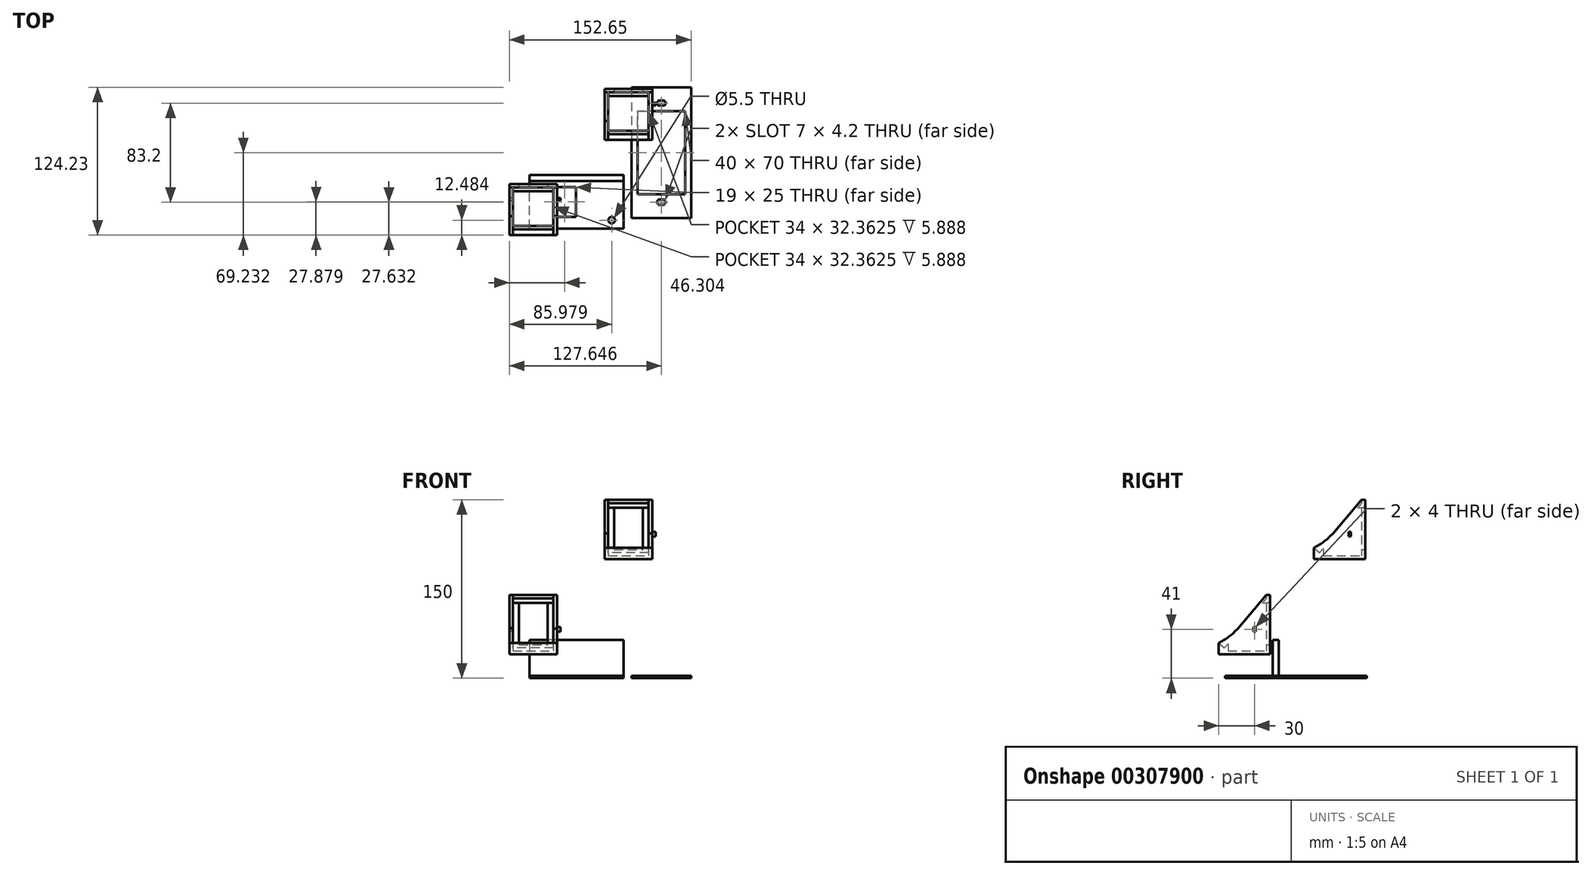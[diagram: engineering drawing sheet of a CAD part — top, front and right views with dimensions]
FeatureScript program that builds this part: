
annotation { "Feature Type Name" : "Feature", "Feature Type Description" : "" }
export const myFeature = defineFeature(function(context is Context, id is Id, definition is map)
    precondition{}
    {
        {
            var Q0;
            Q0=qCreatedBy(makeId("Front.planeOp"),FACE);
            var sketch = newSketch(context, id + "F0", { "sketchPlane" : qUnion([Q0])});
            skLineSegment(sketch, "E0.bottom", {"start": v(-60, 70) * mm, "end": v(-20, 70) * mm});
            skLineSegment(sketch, "E0.top", {"start": v(-60, 20) * mm, "end": v(-20, 20) * mm});
            skLineSegment(sketch, "E0.left", {"start": v(-60, 70) * mm, "end": v(-60, 20) * mm});
            skLineSegment(sketch, "E0.right", {"start": v(-20, 70) * mm, "end": v(-20, 20) * mm});
            skLineSegment(sketch, "E1.bottom", {"start": v(-52, 66) * mm, "end": v(-28, 66) * mm});
            skLineSegment(sketch, "E1.top", {"start": v(-52, 28) * mm, "end": v(-28, 28) * mm});
            skLineSegment(sketch, "E1.left", {"start": v(-52, 66) * mm, "end": v(-52, 28) * mm});
            skLineSegment(sketch, "E1.right", {"start": v(-28, 66) * mm, "end": v(-28, 28) * mm});
            skSolve(sketch);
        }
        {
            var Q0;
            Q0 = qSketchRegion(id + "F0", true);
            extrude(context, id + "F1", {"entities" : qUnion([Q0]), "depth" : 3 * mm});
        }
        {
            var Q0;
            Q0=makeQuery(id+"F1.opExtrude","CAP_FACE",FACE,{"disambiguationData":[OSD([sQuery(id+"F0.wireOp",EDGE,"E0.bottom"),sQuery(id+"F0.wireOp",EDGE,"E0.top"),sQuery(id+"F0.wireOp",EDGE,"E0.left"),sQuery(id+"F0.wireOp",EDGE,"E0.right"),sQuery(id+"F0.wireOp",EDGE,"E1.bottom"),sQuery(id+"F0.wireOp",EDGE,"E1.top"),sQuery(id+"F0.wireOp",EDGE,"E1.left"),sQuery(id+"F0.wireOp",EDGE,"E1.right")])],"isStart":false});
            var sketch = newSketch(context, id + "F2", { "sketchPlane" : qUnion([Q0])});
            skPoint(sketch, "E2.left.start.orphan", {"position": v(-60, 28) * mm});
            skLineSegment(sketch, "E3.bottom", {"start": v(-60, 23) * mm, "end": v(-20, 23) * mm});
            skLineSegment(sketch, "E3.top", {"start": v(-60, 20) * mm, "end": v(-20, 20) * mm});
            skLineSegment(sketch, "E3.left", {"start": v(-60, 23) * mm, "end": v(-60, 20) * mm});
            skLineSegment(sketch, "E3.right", {"start": v(-20, 23) * mm, "end": v(-20, 20) * mm});
            skSolve(sketch);
        }
        {
            var Q0;
            Q0 = qSketchRegion(id + "F2", true);
            extrude(context, id + "F3", {"entities" : qUnion([Q0]), "operationType" : NewBodyOperationType.ADD, "depth" : 40 * mm});
        }
        {
            var Q0;
            Q0=makeQuery(id+"F3.boolean.opBoolean","MERGE",FACE,{"derivedFrom":[makeQuery(id+"F1.opExtrude","SWEPT_FACE",FACE,{"disambiguationData":[OSD([sQuery(id+"F0.wireOp",EDGE,"E0.left")])]}),makeQuery(id+"F3.opExtrude","SWEPT_FACE",FACE,{"disambiguationData":[OSD([sQuery(id+"F2.wireOp",EDGE,"E3.left")])]})]});
            var sketch = newSketch(context, id + "F4", { "sketchPlane" : qUnion([Q0])});
            skLineSegment(sketch, "E4", {"start": v(3, 70) * mm, "end": v(43, 23) * mm});
            skSolve(sketch);
        }
        {
            var Q0;
            Q0=makeQuery(id+"F4.imprint","IMPRINT",FACE,{"disambiguationData":[TD([[makeQuery(id+"F4.imprint","IMPRINT",EDGE,{"derivedFrom":sQuery(id+"F4.wireOp",EDGE,"E4")}),-1.0]])]});
            extrude(context, id + "F5", {"entities" : qUnion([Q0]), "operationType" : NewBodyOperationType.ADD, "oppositeDirection" : true, "depth" : 3 * mm});
        }
        {
            var Q0;
            Q0=makeQuery(id+"F3.boolean.opBoolean","MERGE",FACE,{"derivedFrom":[makeQuery(id+"F1.opExtrude","SWEPT_FACE",FACE,{"disambiguationData":[OSD([sQuery(id+"F0.wireOp",EDGE,"E0.right")])]}),makeQuery(id+"F3.opExtrude","SWEPT_FACE",FACE,{"disambiguationData":[OSD([sQuery(id+"F2.wireOp",EDGE,"E3.right")])]})]});
            var sketch = newSketch(context, id + "F6", { "sketchPlane" : qUnion([Q0])});
            skLineSegment(sketch, "E5", {"start": v(-43, 23) * mm, "end": v(-3, 70) * mm});
            skSolve(sketch);
        }
        {
            var Q0;
            Q0=makeQuery(id+"F6.imprint","IMPRINT",FACE,{"disambiguationData":[TD([[makeQuery(id+"F6.imprint","IMPRINT",EDGE,{"derivedFrom":sQuery(id+"F6.wireOp",EDGE,"E5")}),-1.0]])]});
            extrude(context, id + "F7", {"entities" : qUnion([Q0]), "operationType" : NewBodyOperationType.ADD, "oppositeDirection" : true, "depth" : 3 * mm});
        }
        {
            var Q0;
            Q0=makeQuery(id+"F5.opExtrude","CAP_FACE",FACE,{"disambiguationData":[OSD([sQuery(id+"F0.wireOp",EDGE,"E0.left"),sQuery(id+"F2.wireOp",EDGE,"E3.bottom"),sQuery(id+"F2.wireOp",EDGE,"E3.left"),sQuery(id+"F4.wireOp",EDGE,"E4")])],"isStart":false});
            var sketch = newSketch(context, id + "F8", { "sketchPlane" : qUnion([Q0])});
            skLineSegment(sketch, "E6", {"start": v(-3, 66.91) * mm, "end": v(-6.24, 63.1) * mm});
            skLineSegment(sketch, "E7", {"start": v(-6.24, 63.1) * mm, "end": v(-3, 63.1) * mm});
            skLineSegment(sketch, "E8", {"start": v(-3, 63.1) * mm, "end": v(-3, 66.91) * mm});
            skLineSegment(sketch, "E9.0", {"start": v(-3, 66) * mm, "end": v(0, 66) * mm});
            skLineSegment(sketch, "E10", {"start": v(-3, 63.1) * mm, "end": v(0, 63.1) * mm});
            skLineSegment(sketch, "E11", {"start": v(0, 63.1) * mm, "end": v(0, 66) * mm});
            skSolve(sketch);
        }
        {
            var Q0;
            Q0 = qSketchRegion(id + "F8", true);
            var Q1;
            Q1=makeQuery(id+"F7.opExtrude","CAP_FACE",FACE,{"disambiguationData":[OSD([sQuery(id+"F0.wireOp",EDGE,"E0.right"),sQuery(id+"F2.wireOp",EDGE,"E3.bottom"),sQuery(id+"F2.wireOp",EDGE,"E3.right"),sQuery(id+"F6.wireOp",EDGE,"E5")])],"isStart":false});
            extrude(context, id + "F9", {"entities" : qUnion([Q0]), "operationType" : NewBodyOperationType.ADD, "endBound" : BoundingType.UP_TO_SURFACE, "endBoundEntityFace" : qUnion([Q1]), "depth" : 25 * mm});
        }
        {
            var Q0;
            Q0=makeQuery(id+"F5.opExtrude","CAP_FACE",FACE,{"disambiguationData":[OSD([sQuery(id+"F0.wireOp",EDGE,"E0.left"),sQuery(id+"F2.wireOp",EDGE,"E3.bottom"),sQuery(id+"F2.wireOp",EDGE,"E3.left"),sQuery(id+"F4.wireOp",EDGE,"E4")])],"isStart":false});
            var sketch = newSketch(context, id + "F10", { "sketchPlane" : qUnion([Q0])});
            skLineSegment(sketch, "E12", {"start": v(-35.36, 23) * mm, "end": v(-43, 29.5) * mm});
            skLineSegment(sketch, "E13", {"start": v(-43, 29.5) * mm, "end": v(-43, 23) * mm});
            skLineSegment(sketch, "E14", {"start": v(-43, 23) * mm, "end": v(-35.36, 23) * mm});
            skSolve(sketch);
        }
        {
            var Q0;
            Q0 = qSketchRegion(id + "F10", true);
            var Q1;
            {var subQ0=sQuery(id+"F2.wireOp",EDGE,"E3.right");var subQ1=sQuery(id+"F0.wireOp",EDGE,"E0.right");Q1=makeQuery(id+"F7.boolean.opBoolean","MERGE",FACE,{"derivedFrom":[makeQuery(id+"F3.boolean.opBoolean","MERGE",FACE,{"derivedFrom":[makeQuery(id+"F1.opExtrude","SWEPT_FACE",FACE,{"disambiguationData":[OSD([subQ1])]}),makeQuery(id+"F3.opExtrude","SWEPT_FACE",FACE,{"disambiguationData":[OSD([subQ0])]})]}),makeQuery(id+"F7.opExtrude","CAP_FACE",FACE,{"disambiguationData":[OSD([subQ1,sQuery(id+"F2.wireOp",EDGE,"E3.bottom"),subQ0,sQuery(id+"F6.wireOp",EDGE,"E5")])],"isStart":true})]});}
            var Q2;
            {var subQ0=sQuery(id+"F2.wireOp",EDGE,"E3.left");var subQ1=sQuery(id+"F0.wireOp",EDGE,"E0.left");Q2=makeQuery(id+"F5.boolean.opBoolean","MERGE",FACE,{"derivedFrom":[makeQuery(id+"F3.boolean.opBoolean","MERGE",FACE,{"derivedFrom":[makeQuery(id+"F1.opExtrude","SWEPT_FACE",FACE,{"disambiguationData":[OSD([subQ1])]}),makeQuery(id+"F3.opExtrude","SWEPT_FACE",FACE,{"disambiguationData":[OSD([subQ0])]})]}),makeQuery(id+"F5.opExtrude","CAP_FACE",FACE,{"disambiguationData":[OSD([subQ1,sQuery(id+"F2.wireOp",EDGE,"E3.bottom"),subQ0,sQuery(id+"F4.wireOp",EDGE,"E4")])],"isStart":true})]});}
            extrude(context, id + "F11", {"entities" : qUnion([Q0]), "operationType" : NewBodyOperationType.ADD, "endBound" : BoundingType.UP_TO_SURFACE, "endBoundEntityFace" : qUnion([Q1]), "depth" : 25 * mm, "hasSecondDirection" : true, "secondDirectionBound" : SecondDirectionBoundingType.UP_TO_SURFACE, "secondDirectionOppositeDirection" : true, "secondDirectionBoundEntityFace" : qUnion([Q2]), "secondDirectionDepth" : 25 * mm});
        }
        {
            var Q0;
            Q0=makeQuery(id+"F5.opExtrude","CAP_FACE",FACE,{"disambiguationData":[OSD([sQuery(id+"F0.wireOp",EDGE,"E0.left"),sQuery(id+"F2.wireOp",EDGE,"E3.bottom"),sQuery(id+"F2.wireOp",EDGE,"E3.left"),sQuery(id+"F4.wireOp",EDGE,"E4")])],"isStart":false});
            var sketch = newSketch(context, id + "F12", { "sketchPlane" : qUnion([Q0])});
            skLineSegment(sketch, "E15", {"start": v(-38.27, 25.47) * mm, "end": v(-35.36, 28.89) * mm});
            skLineSegment(sketch, "E16", {"start": v(-35.36, 28.89) * mm, "end": v(-35.36, 23) * mm});
            skSolve(sketch);
        }
        {
            var Q0;
            {var subQ0=sQuery(id+"F12.wireOp",EDGE,"E15");Q0=makeQuery(id+"F12.imprint","IMPRINT",FACE,{"disambiguationData":[TD([[makeQuery(id+"F12.imprint","IMPRINT",EDGE,{"derivedFrom":subQ0}),-1.0]])]});}
            var Q1;
            Q1=makeQuery(id+"F7.opExtrude","CAP_FACE",FACE,{"disambiguationData":[OSD([sQuery(id+"F0.wireOp",EDGE,"E0.right"),sQuery(id+"F2.wireOp",EDGE,"E3.bottom"),sQuery(id+"F2.wireOp",EDGE,"E3.right"),sQuery(id+"F6.wireOp",EDGE,"E5")])],"isStart":false});
            extrude(context, id + "F13", {"entities" : qUnion([Q0]), "operationType" : NewBodyOperationType.ADD, "endBound" : BoundingType.UP_TO_SURFACE, "endBoundEntityFace" : qUnion([Q1]), "depth" : 25 * mm});
        }
        {
            var Q0;
            {var subQ0=sQuery(id+"F6.wireOp",EDGE,"E5");var subQ1=sQuery(id+"F2.wireOp",EDGE,"E3.right");var subQ2=sQuery(id+"F2.wireOp",EDGE,"E3.bottom");var subQ3=sQuery(id+"F0.wireOp",EDGE,"E0.right");Q0=makeQuery(id+"F11.boolean.opBoolean","MERGE",FACE,{"derivedFrom":[makeQuery(id+"F7.boolean.opBoolean","MERGE",FACE,{"derivedFrom":[makeQuery(id+"F3.boolean.opBoolean","MERGE",FACE,{"derivedFrom":[makeQuery(id+"F1.opExtrude","SWEPT_FACE",FACE,{"disambiguationData":[OSD([subQ3])]}),makeQuery(id+"F3.opExtrude","SWEPT_FACE",FACE,{"disambiguationData":[OSD([subQ1])]})]}),makeQuery(id+"F7.opExtrude","CAP_FACE",FACE,{"disambiguationData":[OSD([subQ3,subQ2,subQ1,subQ0])],"isStart":true})]}),makeQuery(id+"F11.opExtrude","CAP_FACE",FACE,{"disambiguationData":[OSD([subQ3,subQ2,subQ1,subQ0])],"isStart":false})]});}
            var sketch = newSketch(context, id + "F14", { "sketchPlane" : qUnion([Q0])});
            skLineSegment(sketch, "E17.bottom", {"start": v(-14, 43) * mm, "end": v(-12, 43) * mm});
            skLineSegment(sketch, "E17.top", {"start": v(-14, 39) * mm, "end": v(-12, 39) * mm});
            skLineSegment(sketch, "E17.left", {"start": v(-14, 43) * mm, "end": v(-14, 39) * mm});
            skLineSegment(sketch, "E17.right", {"start": v(-12, 43) * mm, "end": v(-12, 39) * mm});
            skSolve(sketch);
        }
        {
            var Q0;
            Q0 = qSketchRegion(id + "F14", true);
            extrude(context, id + "F15", {"entities" : qUnion([Q0]), "operationType" : NewBodyOperationType.ADD, "depth" : 3 * mm});
        }
        {
            var Q0;
            {var subQ0=sQuery(id+"F4.wireOp",EDGE,"E4");var subQ1=sQuery(id+"F2.wireOp",EDGE,"E3.left");var subQ2=sQuery(id+"F2.wireOp",EDGE,"E3.bottom");var subQ3=sQuery(id+"F0.wireOp",EDGE,"E0.left");Q0=makeQuery(id+"F11.boolean.opBoolean","MERGE",FACE,{"derivedFrom":[makeQuery(id+"F5.boolean.opBoolean","MERGE",FACE,{"derivedFrom":[makeQuery(id+"F3.boolean.opBoolean","MERGE",FACE,{"derivedFrom":[makeQuery(id+"F1.opExtrude","SWEPT_FACE",FACE,{"disambiguationData":[OSD([subQ3])]}),makeQuery(id+"F3.opExtrude","SWEPT_FACE",FACE,{"disambiguationData":[OSD([subQ1])]})]}),makeQuery(id+"F5.opExtrude","CAP_FACE",FACE,{"disambiguationData":[OSD([subQ3,subQ2,subQ1,subQ0])],"isStart":true})]}),makeQuery(id+"F11.opExtrude","CAP_FACE",FACE,{"disambiguationData":[OSD([subQ3,subQ2,subQ1,subQ0])],"isStart":true})]});}
            var sketch = newSketch(context, id + "F16", { "sketchPlane" : qUnion([Q0])});
            skLineSegment(sketch, "E18.bottom", {"start": v(12, 43) * mm, "end": v(14, 43) * mm});
            skLineSegment(sketch, "E18.top", {"start": v(12, 39) * mm, "end": v(14, 39) * mm});
            skLineSegment(sketch, "E18.left", {"start": v(12, 43) * mm, "end": v(12, 39) * mm});
            skLineSegment(sketch, "E18.right", {"start": v(14, 43) * mm, "end": v(14, 39) * mm});
            skSolve(sketch);
        }
        {
            var Q0;
            Q0 = qSketchRegion(id + "F16", true);
            extrude(context, id + "F17", {"entities" : qUnion([Q0]), "operationType" : NewBodyOperationType.REMOVE, "oppositeDirection" : true, "depth" : 25 * mm});
        }
        {
            var Q0;
            {var subQ0=sQuery(id+"F4.wireOp",EDGE,"E4");var subQ1=sQuery(id+"F2.wireOp",EDGE,"E3.left");var subQ2=sQuery(id+"F2.wireOp",EDGE,"E3.bottom");var subQ3=sQuery(id+"F0.wireOp",EDGE,"E0.left");Q0=makeQuery(id+"F11.boolean.opBoolean","MERGE",FACE,{"derivedFrom":[makeQuery(id+"F5.boolean.opBoolean","MERGE",FACE,{"derivedFrom":[makeQuery(id+"F3.boolean.opBoolean","MERGE",FACE,{"derivedFrom":[makeQuery(id+"F1.opExtrude","SWEPT_FACE",FACE,{"disambiguationData":[OSD([subQ3])]}),makeQuery(id+"F3.opExtrude","SWEPT_FACE",FACE,{"disambiguationData":[OSD([subQ1])]})]}),makeQuery(id+"F5.opExtrude","CAP_FACE",FACE,{"disambiguationData":[OSD([subQ3,subQ2,subQ1,subQ0])],"isStart":true})]}),makeQuery(id+"F11.opExtrude","CAP_FACE",FACE,{"disambiguationData":[OSD([subQ3,subQ2,subQ1,subQ0])],"isStart":true})]});}
            var sketch = newSketch(context, id + "F18", { "sketchPlane" : qUnion([Q0])});
            skArc(sketch, "E19", {"start": v(27.03, 41.77) * mm, "mid": v(34.47, 34.92) * mm, "end": v(43, 29.5) * mm});
            skSolve(sketch);
        }
        {
            var Q0;
            {var subQ0=sQuery(id+"F18.wireOp",EDGE,"E19");Q0=makeQuery(id+"F18.imprint","IMPRINT",FACE,{"disambiguationData":[TD([[makeQuery(id+"F18.imprint","IMPRINT",EDGE,{"derivedFrom":subQ0}),-1.0]])]});}
            var Q1;
            Q1=makeQuery(id+"F5.opExtrude","CAP_FACE",FACE,{"disambiguationData":[OSD([sQuery(id+"F0.wireOp",EDGE,"E0.left"),sQuery(id+"F2.wireOp",EDGE,"E3.bottom"),sQuery(id+"F2.wireOp",EDGE,"E3.left"),sQuery(id+"F4.wireOp",EDGE,"E4")])],"isStart":false});
            extrude(context, id + "F19", {"entities" : qUnion([Q0]), "operationType" : NewBodyOperationType.ADD, "endBound" : BoundingType.UP_TO_SURFACE, "oppositeDirection" : true, "endBoundEntityFace" : qUnion([Q1]), "depth" : 25 * mm});
        }
        {
            var Q0;
            {var subQ0=sQuery(id+"F6.wireOp",EDGE,"E5");var subQ1=sQuery(id+"F2.wireOp",EDGE,"E3.right");var subQ2=sQuery(id+"F2.wireOp",EDGE,"E3.bottom");var subQ3=sQuery(id+"F0.wireOp",EDGE,"E0.right");Q0=makeQuery(id+"F11.boolean.opBoolean","MERGE",FACE,{"derivedFrom":[makeQuery(id+"F7.boolean.opBoolean","MERGE",FACE,{"derivedFrom":[makeQuery(id+"F3.boolean.opBoolean","MERGE",FACE,{"derivedFrom":[makeQuery(id+"F1.opExtrude","SWEPT_FACE",FACE,{"disambiguationData":[OSD([subQ3])]}),makeQuery(id+"F3.opExtrude","SWEPT_FACE",FACE,{"disambiguationData":[OSD([subQ1])]})]}),makeQuery(id+"F7.opExtrude","CAP_FACE",FACE,{"disambiguationData":[OSD([subQ3,subQ2,subQ1,subQ0])],"isStart":true})]}),makeQuery(id+"F11.opExtrude","CAP_FACE",FACE,{"disambiguationData":[OSD([subQ3,subQ2,subQ1,subQ0])],"isStart":false})]});}
            var sketch = newSketch(context, id + "F20", { "sketchPlane" : qUnion([Q0])});
            skArc(sketch, "E20.0", {"start": v(-43, 29.5) * mm, "mid": v(-34.47, 34.92) * mm, "end": v(-27.03, 41.77) * mm});
            skLineSegment(sketch, "E21.0", {"start": v(-39.8, 26.77) * mm, "end": v(-3, 70) * mm});
            skLineSegment(sketch, "E22.0", {"start": v(-39.8, 26.77) * mm, "end": v(-43, 29.5) * mm});
            skSolve(sketch);
        }
        {
            var Q0;
            Q0 = qSketchRegion(id + "F20", true);
            var Q1;
            Q1=makeQuery(id+"F7.opExtrude","CAP_FACE",FACE,{"disambiguationData":[OSD([sQuery(id+"F0.wireOp",EDGE,"E0.right"),sQuery(id+"F2.wireOp",EDGE,"E3.bottom"),sQuery(id+"F2.wireOp",EDGE,"E3.right"),sQuery(id+"F6.wireOp",EDGE,"E5")])],"isStart":false});
            extrude(context, id + "F21", {"entities" : qUnion([Q0]), "operationType" : NewBodyOperationType.ADD, "endBound" : BoundingType.UP_TO_SURFACE, "oppositeDirection" : true, "endBoundEntityFace" : qUnion([Q1]), "depth" : 25 * mm});
        }
        {
            var Q0;
            Q0=makeQuery(id+"F1.opExtrude","SWEPT_BODY",BODY,{"disambiguationData":[OSD([sQuery(id+"F0.wireOp",EDGE,"E0.bottom"),sQuery(id+"F0.wireOp",EDGE,"E0.top"),sQuery(id+"F0.wireOp",EDGE,"E0.left"),sQuery(id+"F0.wireOp",EDGE,"E0.right"),sQuery(id+"F0.wireOp",EDGE,"E1.bottom"),sQuery(id+"F0.wireOp",EDGE,"E1.top"),sQuery(id+"F0.wireOp",EDGE,"E1.left"),sQuery(id+"F0.wireOp",EDGE,"E1.right")])]});
            transform(context, id + "F22", {"entities" : qUnion([Q0]), "transformType" : TransformType.TRANSLATION_3D, "dx" : 80 * mm, "dy" : 80 * mm, "dz" : 80 * mm, "makeCopy" : true});
        }
        {
            var Q0;
            {var subQ0=sQuery(id+"F4.wireOp",EDGE,"E4");var subQ1=sQuery(id+"F2.wireOp",EDGE,"E3.left");var subQ2=sQuery(id+"F2.wireOp",EDGE,"E3.bottom");var subQ3=sQuery(id+"F0.wireOp",EDGE,"E0.left");Q0=makeQuery(id+"F22.opPattern","COPY",FACE,{"derivedFrom":makeQuery(id+"F19.boolean.opBoolean","MERGE",FACE,{"derivedFrom":[makeQuery(id+"F11.boolean.opBoolean","MERGE",FACE,{"derivedFrom":[makeQuery(id+"F5.boolean.opBoolean","MERGE",FACE,{"derivedFrom":[makeQuery(id+"F3.boolean.opBoolean","MERGE",FACE,{"derivedFrom":[makeQuery(id+"F1.opExtrude","SWEPT_FACE",FACE,{"disambiguationData":[OSD([subQ3])]}),makeQuery(id+"F3.opExtrude","SWEPT_FACE",FACE,{"disambiguationData":[OSD([subQ1])]})]}),makeQuery(id+"F5.opExtrude","CAP_FACE",FACE,{"disambiguationData":[OSD([subQ3,subQ2,subQ1,subQ0])],"isStart":true})]}),makeQuery(id+"F11.opExtrude","CAP_FACE",FACE,{"disambiguationData":[OSD([subQ3,subQ2,subQ1,subQ0])],"isStart":true})]}),makeQuery(id+"F19.opExtrude","CAP_FACE",FACE,{"disambiguationData":[OSD([subQ3,subQ2,subQ1,subQ0,sQuery(id+"F10.wireOp",EDGE,"E12"),sQuery(id+"F18.wireOp",EDGE,"E19")])],"isStart":true})]}),"instanceName":"1"});}
            var sketch = newSketch(context, id + "F23", { "sketchPlane" : qUnion([Q0])});
            skLineSegment(sketch, "E23.0", {"start": v(-68, 123) * mm, "end": v(-68, 119) * mm});
            skPoint(sketch, "E24.0", {"position": v(-67, 123) * mm});
            skLineSegment(sketch, "E25.0", {"start": v(-68, 123) * mm, "end": v(-66, 123) * mm});
            skLineSegment(sketch, "E26.0", {"start": v(-66, 123) * mm, "end": v(-66, 119) * mm});
            skLineSegment(sketch, "E27.0", {"start": v(-68, 119) * mm, "end": v(-66, 119) * mm});
            skSolve(sketch);
        }
        {
            var Q0;
            Q0 = qSketchRegion(id + "F23", true);
            var Q1;
            {var subQ0=sQuery(id+"F4.wireOp",EDGE,"E4");var subQ1=sQuery(id+"F2.wireOp",EDGE,"E3.left");var subQ2=sQuery(id+"F2.wireOp",EDGE,"E3.bottom");var subQ3=sQuery(id+"F0.wireOp",EDGE,"E0.left");Q1=makeQuery(id+"F22.opPattern","COPY",FACE,{"derivedFrom":makeQuery(id+"F19.boolean.opBoolean","MERGE",FACE,{"derivedFrom":[makeQuery(id+"F5.opExtrude","CAP_FACE",FACE,{"disambiguationData":[OSD([subQ3,subQ2,subQ1,subQ0])],"isStart":false}),makeQuery(id+"F19.opExtrude","CAP_FACE",FACE,{"disambiguationData":[OSD([subQ3,subQ2,subQ1,subQ0])],"isStart":false})]}),"instanceName":"1"});}
            extrude(context, id + "F24", {"entities" : qUnion([Q0]), "operationType" : NewBodyOperationType.ADD, "endBound" : BoundingType.UP_TO_SURFACE, "oppositeDirection" : true, "endBoundEntityFace" : qUnion([Q1]), "depth" : 25 * mm});
        }
        {
            var Q0;
            Q0=qCreatedBy(makeId("Top.planeOp"),FACE);
            var sketch = newSketch(context, id + "F25", { "sketchPlane" : qUnion([Q0])});
            skLineSegment(sketch, "E28.bottom", {"start": v(42.65, 81.23) * mm, "end": v(92.65, 81.23) * mm});
            skLineSegment(sketch, "E28.top", {"start": v(42.65, -28.77) * mm, "end": v(92.65, -28.77) * mm});
            skLineSegment(sketch, "E28.left", {"start": v(42.65, 81.23) * mm, "end": v(42.65, -28.77) * mm});
            skLineSegment(sketch, "E28.right", {"start": v(92.65, 81.23) * mm, "end": v(92.65, -28.77) * mm});
            skSolve(sketch);
        }
        {
            var Q0;
            Q0=makeQuery(id+"F25.imprint","IMPRINT",FACE,{"disambiguationData":[TD([[makeQuery(id+"F25.imprint","IMPRINT",EDGE,{"derivedFrom":sQuery(id+"F25.wireOp",EDGE,"E28.bottom")}),-1.0]])]});
            extrude(context, id + "F26", {"entities" : qUnion([Q0]), "depth" : 2 * mm});
        }
        {
            var Q0;
            Q0=makeQuery(id+"F26.opExtrude","CAP_FACE",FACE,{"disambiguationData":[OSD([sQuery(id+"F25.wireOp",EDGE,"E28.bottom"),sQuery(id+"F25.wireOp",EDGE,"E28.top"),sQuery(id+"F25.wireOp",EDGE,"E28.left"),sQuery(id+"F25.wireOp",EDGE,"E28.right")])],"isStart":true});
            var sketch = newSketch(context, id + "F27", { "sketchPlane" : qUnion([Q0])});
            skLineSegment(sketch, "E29.bottom", {"start": v(87.65, -61.23) * mm, "end": v(47.65, -61.23) * mm});
            skLineSegment(sketch, "E29.top", {"start": v(87.65, 8.77) * mm, "end": v(47.65, 8.77) * mm});
            skLineSegment(sketch, "E29.left", {"start": v(87.65, -61.23) * mm, "end": v(87.65, 8.77) * mm});
            skLineSegment(sketch, "E29.right", {"start": v(47.65, -61.23) * mm, "end": v(47.65, 8.77) * mm});
            skLineSegment(sketch, "E30", {"start": v(87.65, -35.53) * mm, "end": v(92.65, -35.53) * mm});
            skLineSegment(sketch, "E31", {"start": v(47.65, -35.53) * mm, "end": v(42.65, -35.53) * mm});
            skLineSegment(sketch, "E32", {"start": v(63.6, -61.23) * mm, "end": v(63.6, -81.23) * mm});
            skPoint(sketch, "E32.endSnap0", {"position": v(67.65, -81.23) * mm});
            skLineSegment(sketch, "E33", {"start": v(62.82, 8.77) * mm, "end": v(62.82, 28.77) * mm});
            skSolve(sketch);
        }
        {
            var Q0;
            Q0 = qSketchRegion(id + "F27", true);
            extrude(context, id + "F28", {"entities" : qUnion([Q0]), "operationType" : NewBodyOperationType.REMOVE, "oppositeDirection" : true, "depth" : 25 * mm});
        }
        {
            var Q0;
            Q0=makeQuery(id+"F26.opExtrude","CAP_FACE",FACE,{"disambiguationData":[OSD([sQuery(id+"F25.wireOp",EDGE,"E28.bottom"),sQuery(id+"F25.wireOp",EDGE,"E28.top"),sQuery(id+"F25.wireOp",EDGE,"E28.left"),sQuery(id+"F25.wireOp",EDGE,"E28.right")])],"isStart":true});
            var sketch = newSketch(context, id + "F29", { "sketchPlane" : qUnion([Q0])});
            skLineSegment(sketch, "E34.bottom", {"start": v(71.15, -69.93) * mm, "end": v(64.15, -69.93) * mm});
            skLineSegment(sketch, "E34.top", {"start": v(71.15, -65.73) * mm, "end": v(64.15, -65.73) * mm});
            skLineSegment(sketch, "E34.left", {"start": v(71.15, -69.93) * mm, "end": v(71.15, -65.73) * mm});
            skLineSegment(sketch, "E34.right", {"start": v(64.15, -69.93) * mm, "end": v(64.15, -65.73) * mm});
            skLineSegment(sketch, "E35", {"start": v(71.15, -67.83) * mm, "end": v(92.65, -67.83) * mm});
            skLineSegment(sketch, "E36", {"start": v(64.15, -67.83) * mm, "end": v(42.65, -67.83) * mm});
            skArc(sketch, "E37", {"start": v(70.15, -69.93) * mm, "mid": v(71.15, -67.83) * mm, "end": v(70.15, -65.73) * mm});
            skArc(sketch, "E38", {"start": v(65.15, -65.73) * mm, "mid": v(64.15, -67.83) * mm, "end": v(65.15, -69.93) * mm});
            skLineSegment(sketch, "E39", {"start": v(70.15, -65.73) * mm, "end": v(70.15, -69.93) * mm});
            skLineSegment(sketch, "E40", {"start": v(65.15, -69.93) * mm, "end": v(65.15, -65.73) * mm});
            skLineSegment(sketch, "E41", {"start": v(92.65, -26.23) * mm, "end": v(42.65, -26.23) * mm});
            skLineSegment(sketch, "E42.MirrorCS", {"start": v(65.15, 17.47) * mm, "end": v(65.15, 13.27) * mm});
            skLineSegment(sketch, "E43.MirrorCS", {"start": v(70.15, 13.27) * mm, "end": v(70.15, 17.47) * mm});
            skArc(sketch, "E44.MirrorCS", {"start": v(70.15, 17.47) * mm, "mid": v(71.15, 15.37) * mm, "end": v(70.15, 13.27) * mm});
            skArc(sketch, "E45.MirrorCS", {"start": v(65.15, 13.27) * mm, "mid": v(64.15, 15.37) * mm, "end": v(65.15, 17.47) * mm});
            skLineSegment(sketch, "E46.MirrorCS", {"start": v(71.15, 13.27) * mm, "end": v(64.15, 13.27) * mm});
            skLineSegment(sketch, "E47.MirrorCS", {"start": v(64.15, 17.47) * mm, "end": v(64.15, 13.27) * mm});
            skLineSegment(sketch, "E48.MirrorCS", {"start": v(71.15, 17.47) * mm, "end": v(71.15, 13.27) * mm});
            skLineSegment(sketch, "E49.MirrorCS", {"start": v(71.15, 17.47) * mm, "end": v(64.15, 17.47) * mm});
            skSolve(sketch);
        }
        {
            var Q0;
            {var subQ0=sQuery(id+"F29.wireOp",EDGE,"E43.MirrorCS");Q0=makeQuery(id+"F29.imprint","IMPRINT",FACE,{"disambiguationData":[TD([[makeQuery(id+"F29.imprint","IMPRINT",EDGE,{"derivedFrom":subQ0}),-1.0]])]});}
            var Q1;
            {var subQ0=sQuery(id+"F29.wireOp",EDGE,"E42.MirrorCS");Q1=makeQuery(id+"F29.imprint","IMPRINT",FACE,{"disambiguationData":[TD([[makeQuery(id+"F29.imprint","IMPRINT",EDGE,{"derivedFrom":subQ0}),1.0]])]});}
            var Q2;
            {var subQ0=sQuery(id+"F29.wireOp",EDGE,"E42.MirrorCS");Q2=makeQuery(id+"F29.imprint","IMPRINT",FACE,{"disambiguationData":[TD([[makeQuery(id+"F29.imprint","IMPRINT",EDGE,{"derivedFrom":subQ0}),-1.0]])]});}
            var Q3;
            {var subQ0=sQuery(id+"F29.wireOp",EDGE,"E39");Q3=makeQuery(id+"F29.imprint","IMPRINT",FACE,{"disambiguationData":[TD([[makeQuery(id+"F29.imprint","IMPRINT",EDGE,{"derivedFrom":subQ0}),-1.0]])]});}
            var Q4;
            {var subQ2=sQuery(id+"F29.wireOp",EDGE,"E39");Q4=makeQuery(id+"F29.imprint","IMPRINT",FACE,{"disambiguationData":[TD([[makeQuery(id+"F29.imprint","IMPRINT",EDGE,{"derivedFrom":subQ2}),1.0]])]});}
            var Q5;
            {var subQ2=sQuery(id+"F29.wireOp",EDGE,"E40");Q5=makeQuery(id+"F29.imprint","IMPRINT",FACE,{"disambiguationData":[TD([[makeQuery(id+"F29.imprint","IMPRINT",EDGE,{"derivedFrom":subQ2}),1.0]])]});}
            extrude(context, id + "F30", {"entities" : qUnion([Q0, Q1, Q2, Q3, Q4, Q5]), "operationType" : NewBodyOperationType.REMOVE, "oppositeDirection" : true, "depth" : 25 * mm});
        }
        {
            var Q0;
            Q0=qCreatedBy(makeId("Top.planeOp"),FACE);
            var sketch = newSketch(context, id + "F31", { "sketchPlane" : qUnion([Q0])});
            skLineSegment(sketch, "E50.bottom", {"start": v(-23.2, -27.62) * mm, "end": v(-4.2, -27.62) * mm});
            skLineSegment(sketch, "E50.top", {"start": v(-23.2, -2.62) * mm, "end": v(-4.2, -2.62) * mm});
            skLineSegment(sketch, "E50.left", {"start": v(-23.2, -27.62) * mm, "end": v(-23.2, -2.62) * mm});
            skLineSegment(sketch, "E50.right", {"start": v(-4.2, -27.62) * mm, "end": v(-4.2, -2.62) * mm});
            skSolve(sketch);
        }
        {
            var Q0;
            Q0=makeQuery(id+"F31.imprint","IMPRINT",FACE,{"disambiguationData":[TD([[makeQuery(id+"F31.imprint","IMPRINT",EDGE,{"derivedFrom":sQuery(id+"F31.wireOp",EDGE,"E50.bottom")}),1.0]])]});
            var sketch = newSketch(context, id + "F32", { "sketchPlane" : qUnion([Q0])});
            skLineSegment(sketch, "E51.bottom", {"start": v(-43.2, -37.62) * mm, "end": v(35.8, -37.62) * mm});
            skLineSegment(sketch, "E51.top", {"start": v(-43.2, 7.38) * mm, "end": v(35.8, 7.38) * mm});
            skLineSegment(sketch, "E51.left", {"start": v(-43.2, -37.62) * mm, "end": v(-43.2, 7.38) * mm});
            skLineSegment(sketch, "E51.right", {"start": v(35.8, -37.62) * mm, "end": v(35.8, 7.38) * mm});
            skSolve(sketch);
        }
        {
            var Q0;
            Q0=makeQuery(id+"F32.imprint","IMPRINT",FACE,{"disambiguationData":[TD([[makeQuery(id+"F32.imprint","IMPRINT",EDGE,{"derivedFrom":sQuery(id+"F32.wireOp",EDGE,"E51.bottom")}),1.0]])]});
            extrude(context, id + "F33", {"entities" : qUnion([Q0]), "depth" : 2 * mm});
        }
        {
            var Q0;
            Q0=makeQuery(id+"F33.opExtrude","CAP_FACE",FACE,{"disambiguationData":[OSD([sQuery(id+"F31.wireOp",EDGE,"E50.bottom"),sQuery(id+"F31.wireOp",EDGE,"E50.top"),sQuery(id+"F31.wireOp",EDGE,"E50.left"),sQuery(id+"F31.wireOp",EDGE,"E50.right"),sQuery(id+"F32.wireOp",EDGE,"E51.bottom"),sQuery(id+"F32.wireOp",EDGE,"E51.top"),sQuery(id+"F32.wireOp",EDGE,"E51.left"),sQuery(id+"F32.wireOp",EDGE,"E51.right")])],"isStart":false});
            var sketch = newSketch(context, id + "F34", { "sketchPlane" : qUnion([Q0])});
            skLineSegment(sketch, "E52.bottom", {"start": v(35.8, 2.38) * mm, "end": v(-43.2, 2.38) * mm});
            skLineSegment(sketch, "E52.top", {"start": v(35.8, 7.38) * mm, "end": v(-43.2, 7.38) * mm});
            skLineSegment(sketch, "E52.left", {"start": v(35.8, 2.38) * mm, "end": v(35.8, 7.38) * mm});
            skLineSegment(sketch, "E52.right", {"start": v(-43.2, 2.38) * mm, "end": v(-43.2, 7.38) * mm});
            skSolve(sketch);
        }
        {
            var Q0;
            Q0 = qSketchRegion(id + "F34", true);
            extrude(context, id + "F35", {"entities" : qUnion([Q0]), "operationType" : NewBodyOperationType.ADD, "depth" : 30 * mm});
        }
        {
            var Q0;
            Q0=makeQuery(id+"F33.opExtrude","CAP_FACE",FACE,{"disambiguationData":[OSD([sQuery(id+"F31.wireOp",EDGE,"E50.bottom"),sQuery(id+"F31.wireOp",EDGE,"E50.top"),sQuery(id+"F31.wireOp",EDGE,"E50.left"),sQuery(id+"F31.wireOp",EDGE,"E50.right"),sQuery(id+"F32.wireOp",EDGE,"E51.bottom"),sQuery(id+"F32.wireOp",EDGE,"E51.top"),sQuery(id+"F32.wireOp",EDGE,"E51.left"),sQuery(id+"F32.wireOp",EDGE,"E51.right")])],"isStart":true});
            var sketch = newSketch(context, id + "F36", { "sketchPlane" : qUnion([Q0])});
            skCircle(sketch, "E53", {"center": v(25.98, 30.52) * mm, "radius": 2.75 * mm});
            skSolve(sketch);
        }
        {
            var Q0;
            Q0 = qSketchRegion(id + "F36", true);
            extrude(context, id + "F37", {"entities" : qUnion([Q0]), "operationType" : NewBodyOperationType.REMOVE, "oppositeDirection" : true, "depth" : 25 * mm});
        }
    });
